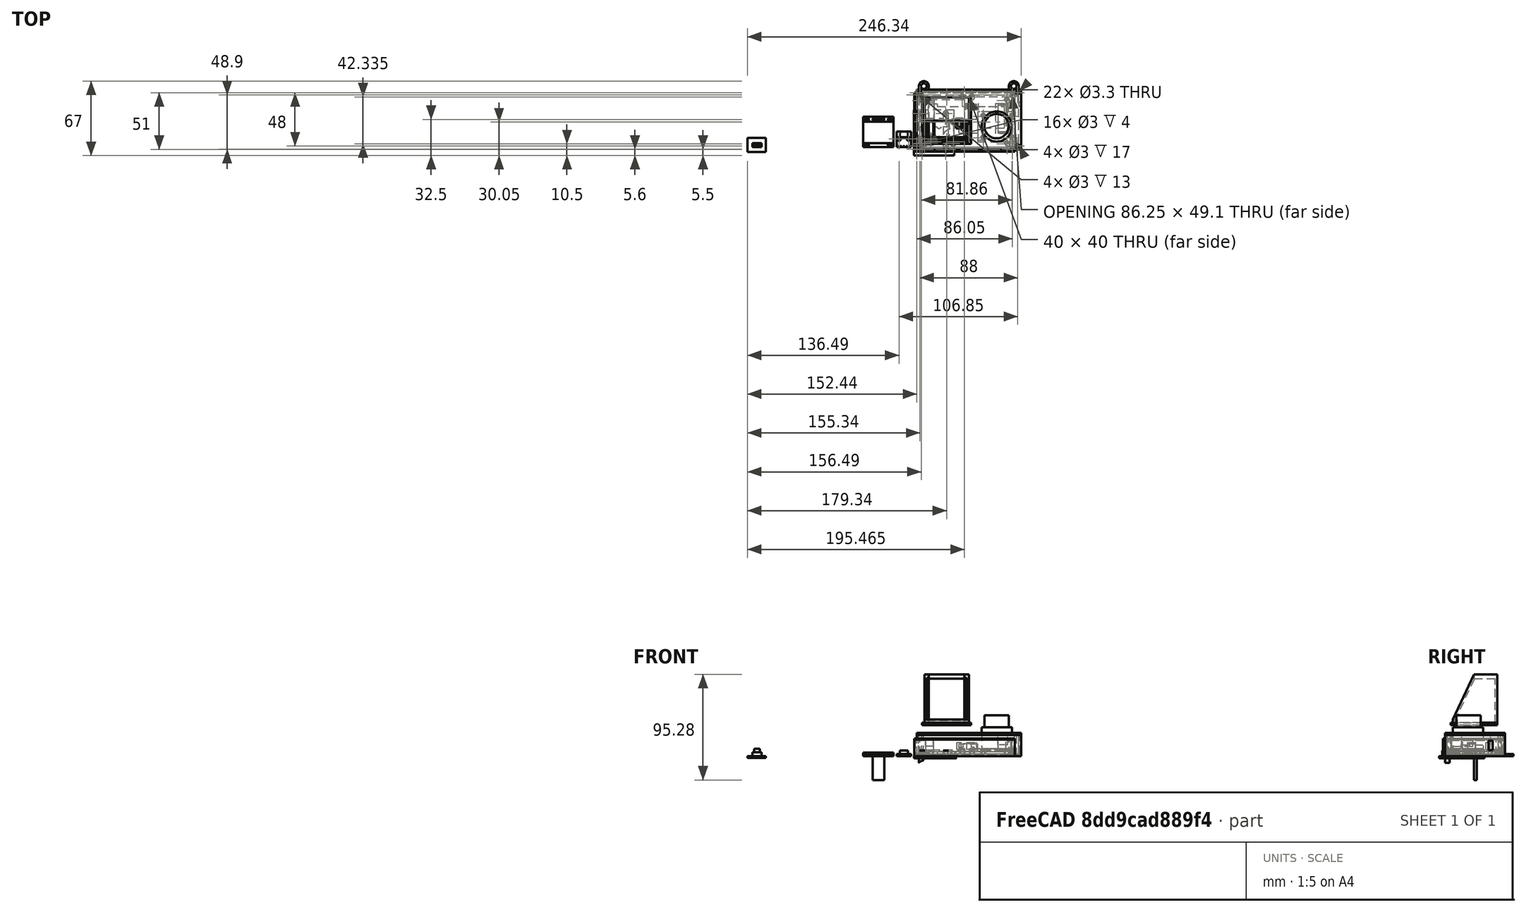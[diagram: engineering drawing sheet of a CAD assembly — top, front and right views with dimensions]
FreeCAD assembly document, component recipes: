
FREECAD ASSEMBLY — COMPONENT RECIPES ("TredmillConrollerHousing_v5")

This assembly document has 8 components, labeled P0..P7 below (a component is one placed body or linked part). 0 of them carry a construction recipe — the FreeCAD feature program that regenerates the part from scratch, quoted from this document or its linked companion documents; the rest are supplied as boundary geometry only. No exploded tour is included for this assembly.
COMPONENT P0 — geometry summary ("Link_Switck"; no construction recipe available for this part):
  bounding box: 16.7 x 12.7 x 8.2 mm
  tessellated surface: 44 triangles
  volume: 486 mm^3 (28% of its bounding box)
COMPONENT P1 — geometry summary ("Fusion_JoyStick_connector001"; no construction recipe available for this part):
  bounding box: 50.8 x 31.9 x 27.2 mm
  tessellated surface: 3,076 triangles
  volume: 17722 mm^3 (40% of its bounding box)
COMPONENT P2 — geometry summary ("Fusion_MicroUSBBreakout001"; no construction recipe available for this part):
  bounding box: 14.2 x 13.0 x 5.0 mm
  tessellated surface: 1,868 triangles
  volume: 447 mm^3 (49% of its bounding box)
  symmetry: mirror-symmetric across its x mid-plane
COMPONENT P3 — geometry summary ("Fusion_diplayAndConnector001"; no construction recipe available for this part):
  bounding box: 31.9 x 27.3 x 25.2 mm
  tessellated surface: 2,772 triangles
  volume: 2370 mm^3 (11% of its bounding box)
  symmetry: mirror-symmetric across its x mid-plane
COMPONENT P4 — geometry summary ("Cut_MainBoardCase_JoyStick_StandWitHole001"; no construction recipe available for this part):
  bounding box: 31.0 x 24.6 x 4.0 mm
  tessellated surface: 4,032 triangles
  volume: 201 mm^3 (7% of its bounding box)
  symmetry: 2-fold rotationally symmetric about the x axis; 2-fold rotationally symmetric about the y axis; 2-fold rotationally symmetric about the z axis; mirror-symmetric across its x mid-plane, y mid-plane, z mid-plane
COMPONENT P5 — geometry summary ("Cut_MicroUSBBreakout_stand001"; no construction recipe available for this part):
  bounding box: 13.7 x 5.0 x 4.0 mm
  tessellated surface: 2,016 triangles
  volume: 101 mm^3 (37% of its bounding box)
  symmetry: 2-fold rotationally symmetric about the x axis; 2-fold rotationally symmetric about the y axis; 2-fold rotationally symmetric about the z axis; mirror-symmetric across its x mid-plane, y mid-plane, z mid-plane
COMPONENT P6 — geometry summary ("Extrude_DisplayCase_Side001"; no construction recipe available for this part):
  bounding box: 45.8 x 40.0 x 4.0 mm
  tessellated surface: 20 triangles
  volume: 5774 mm^3 (79% of its bounding box)
  symmetry: mirror-symmetric across its x mid-plane
COMPONENT P7 — geometry summary ("Fusion_DisplayCase_Front001"; no construction recipe available for this part):
  bounding box: 38.0 x 36.0 x 19.1 mm
  tessellated surface: 2,088 triangles
  volume: 1739 mm^3 (7% of its bounding box)
  symmetry: mirror-symmetric across its x mid-plane
PROVENANCE & LICENSES
A FreeCAD (.FCStd) document from a public repository crawl; recipes are the document's own serialized feature recipes (and, for linked parts, companion documents' recipes).
License: as declared in the source repository (recorded in the dataset sidecar).
